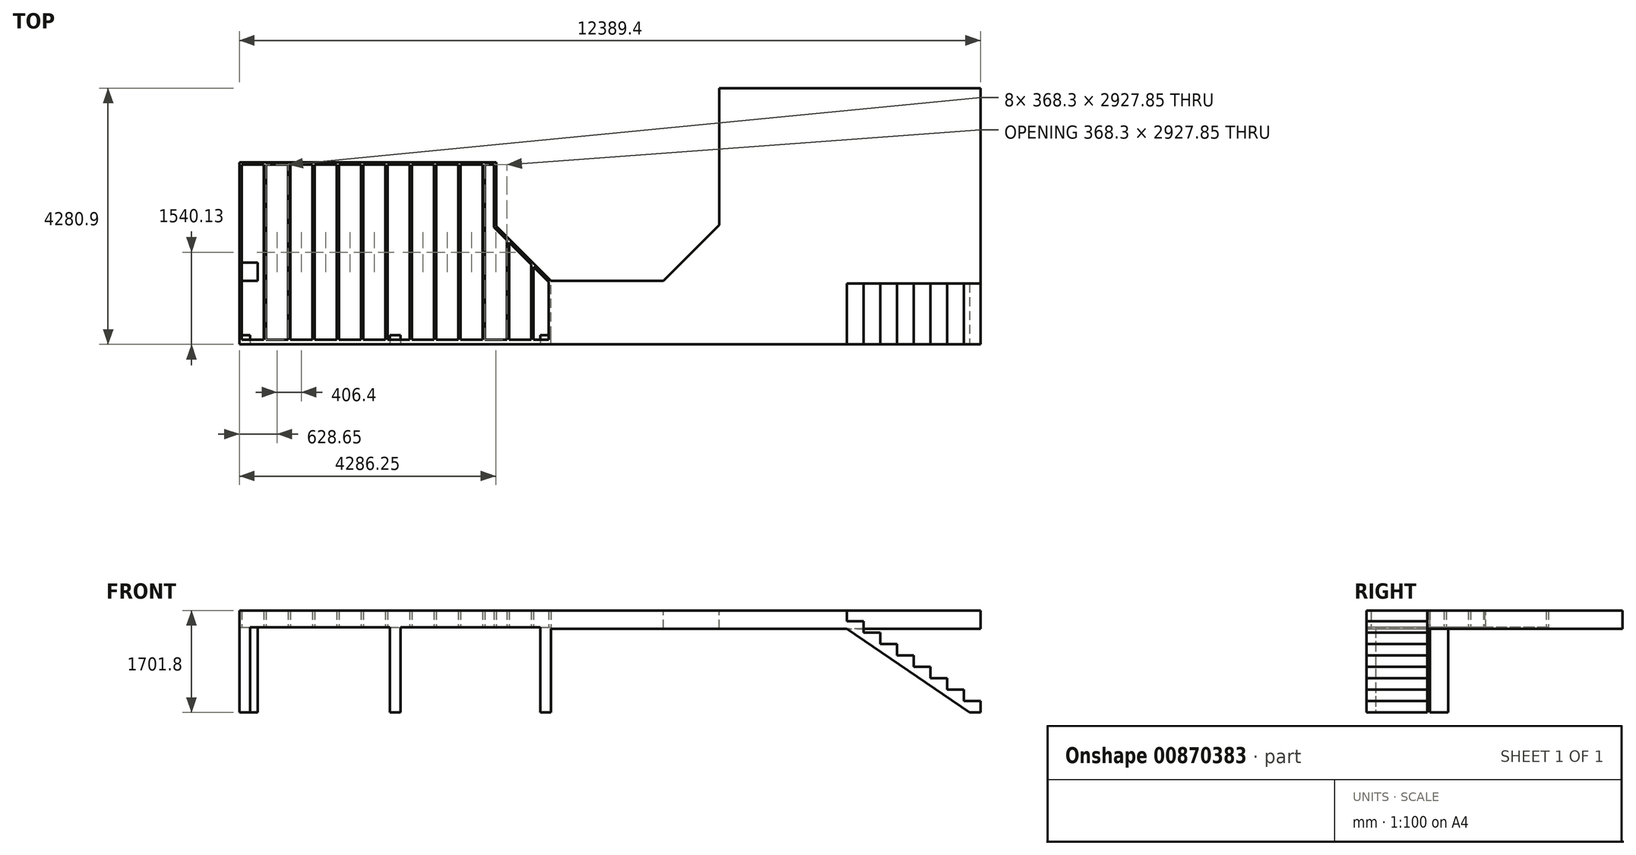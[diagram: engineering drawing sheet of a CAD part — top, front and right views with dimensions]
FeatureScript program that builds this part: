
annotation { "Feature Type Name" : "Feature", "Feature Type Description" : "" }
export const myFeature = defineFeature(function(context is Context, id is Id, definition is map)
    precondition{}
    {
        {
            var Q0;
            Q0=qCreatedBy(makeId("Top.planeOp"),FACE);
            var sketch = newSketch(context, id + "F0", { "sketchPlane" : qUnion([Q0])});
            skLineSegment(sketch, "E0.bottom", {"start": v(0, -1676.4) * mm, "end": v(304.8, -1676.4) * mm});
            skLineSegment(sketch, "E0.top", {"start": v(0, -1981.2) * mm, "end": v(304.8, -1981.2) * mm});
            skLineSegment(sketch, "E0.left", {"start": v(0, -1676.4) * mm, "end": v(0, -1981.2) * mm});
            skLineSegment(sketch, "E0.right", {"start": v(304.8, -1676.4) * mm, "end": v(304.8, -1981.2) * mm});
            skLineSegment(sketch, "E1.bottom", {"start": v(0, -2889.75) * mm, "end": v(177.8, -2889.75) * mm});
            skLineSegment(sketch, "E1.top", {"start": v(0, -3042.15) * mm, "end": v(177.8, -3042.15) * mm});
            skLineSegment(sketch, "E1.left", {"start": v(0, -2889.75) * mm, "end": v(0, -3042.15) * mm});
            skLineSegment(sketch, "E1.right", {"start": v(177.8, -2889.75) * mm, "end": v(177.8, -3042.15) * mm});
            skLineSegment(sketch, "E2.bottom", {"start": v(2514.6, -2889.75) * mm, "end": v(2692.4, -2889.75) * mm});
            skLineSegment(sketch, "E2.top", {"start": v(2514.6, -3042.15) * mm, "end": v(2692.4, -3042.15) * mm});
            skLineSegment(sketch, "E2.left", {"start": v(2514.6, -2889.75) * mm, "end": v(2514.6, -3042.15) * mm});
            skLineSegment(sketch, "E2.right", {"start": v(2692.4, -2889.75) * mm, "end": v(2692.4, -3042.15) * mm});
            skLineSegment(sketch, "E3.bottom", {"start": v(5029.2, -2889.75) * mm, "end": v(5207, -2889.75) * mm});
            skLineSegment(sketch, "E3.top", {"start": v(5029.2, -3042.15) * mm, "end": v(5207, -3042.15) * mm});
            skLineSegment(sketch, "E3.left", {"start": v(5029.2, -2889.75) * mm, "end": v(5029.2, -3042.15) * mm});
            skLineSegment(sketch, "E3.right", {"start": v(5207, -2889.75) * mm, "end": v(5207, -3042.15) * mm});
            skLineSegment(sketch, "E4", {"start": v(0, 0) * mm, "end": v(4292.6, 0) * mm, "construction": true});
            skLineSegment(sketch, "E5", {"start": v(4292.6, 0) * mm, "end": v(4292.6, -1066.8) * mm, "construction": true});
            skLineSegment(sketch, "E6", {"start": v(4292.6, -1066.8) * mm, "end": v(5226.55, -2000.75) * mm, "construction": true});
            skLineSegment(sketch, "E7", {"start": v(5226.55, -2000.75) * mm, "end": v(7106.15, -2000.75) * mm, "construction": true});
            skSolve(sketch);
        }
        {
            var Q0;
            Q0=qSketchRegion(id+"F0",true);
            extrude(context, id + "F1", {"entities" : qUnion([Q0]), "depth" : 1422.4 * mm, "offsetDistance" : 25.4 * mm});
        }
        {
            var Q0;
            Q0=makeQuery(id+"F1.opExtrude","CAP_FACE",FACE,{"disambiguationData":[OSD([sQuery(id+"F0.wireOp",EDGE,"E0.bottom"),sQuery(id+"F0.wireOp",EDGE,"E0.top"),sQuery(id+"F0.wireOp",EDGE,"E0.left"),sQuery(id+"F0.wireOp",EDGE,"E0.right")])],"isStart":false});
            var sketch = newSketch(context, id + "F2", { "sketchPlane" : qUnion([Q0])});
            skLineSegment(sketch, "E8.0", {"start": v(0, 0) * mm, "end": v(4292.6, 0) * mm});
            skLineSegment(sketch, "E9.0", {"start": v(4292.6, 0) * mm, "end": v(4292.6, -1066.8) * mm});
            skLineSegment(sketch, "E9.1", {"start": v(4292.6, -1066.8) * mm, "end": v(5207, -1981.2) * mm});
            skLineSegment(sketch, "E10", {"start": v(0, 0) * mm, "end": v(0, -3042.15) * mm});
            skLineSegment(sketch, "E11", {"start": v(0, -3042.15) * mm, "end": v(5207, -3042.15) * mm});
            skLineSegment(sketch, "E12", {"start": v(5207, -3042.15) * mm, "end": v(5207, -1981.2) * mm});
            skPoint(sketch, "E13.orphan", {"position": v(5226.55, -2000.75) * mm});
            skLineSegment(sketch, "E14.0", {"start": v(4254.5, -38.1) * mm, "end": v(4254.5, -1082.58) * mm});
            skLineSegment(sketch, "E14.1", {"start": v(5168.9, -3004.05) * mm, "end": v(5168.9, -1996.98) * mm});
            skLineSegment(sketch, "E14.2", {"start": v(38.1, -3004.05) * mm, "end": v(5168.9, -3004.05) * mm});
            skLineSegment(sketch, "E14.3", {"start": v(4254.5, -1082.58) * mm, "end": v(5168.9, -1996.98) * mm});
            skLineSegment(sketch, "E14.4", {"start": v(38.1, -38.1) * mm, "end": v(38.1, -3004.05) * mm});
            skLineSegment(sketch, "E14.5", {"start": v(38.1, -38.1) * mm, "end": v(4254.5, -38.1) * mm});
            skSolve(sketch);
        }
        {
            var Q0;
            Q0=qSketchRegion(id+"F2",true);
            extrude(context, id + "F3", {"entities" : qUnion([Q0]), "operationType" : NewBodyOperationType.ADD, "depth" : 279.4 * mm, "offsetDistance" : 25.4 * mm});
        }
        {
            var Q0;
            Q0=makeQuery(id+"F1.opExtrude","CAP_FACE",FACE,{"disambiguationData":[OSD([sQuery(id+"F0.wireOp",EDGE,"E1.bottom"),sQuery(id+"F0.wireOp",EDGE,"E1.top"),sQuery(id+"F0.wireOp",EDGE,"E1.left"),sQuery(id+"F0.wireOp",EDGE,"E1.right")])],"isStart":false});
            var sketch = newSketch(context, id + "F4", { "sketchPlane" : qUnion([Q0])});
            skPoint(sketch, "E15.oppositeSnap0", {"position": v(38.1, -2965.95) * mm});
            skLineSegment(sketch, "E15.bottom", {"start": v(38.1, -3004.05) * mm, "end": v(5168.9, -3004.05) * mm});
            skLineSegment(sketch, "E15.top", {"start": v(38.1, -2965.95) * mm, "end": v(5168.9, -2965.95) * mm});
            skLineSegment(sketch, "E15.left", {"start": v(38.1, -3004.05) * mm, "end": v(38.1, -2965.95) * mm});
            skLineSegment(sketch, "E15.right", {"start": v(5168.9, -3004.05) * mm, "end": v(5168.9, -2965.95) * mm});
            skSolve(sketch);
        }
        {
            var Q0;
            Q0=qSketchRegion(id+"F4",true);
            var Q1;
            Q1=makeQuery(id+"F3.opExtrude","CAP_FACE",FACE,{"disambiguationData":[OSD([sQuery(id+"F2.wireOp",EDGE,"E8.0"),sQuery(id+"F2.wireOp",EDGE,"E9.0"),sQuery(id+"F2.wireOp",EDGE,"E9.1"),sQuery(id+"F2.wireOp",EDGE,"E10"),sQuery(id+"F2.wireOp",EDGE,"E11"),sQuery(id+"F2.wireOp",EDGE,"E12"),sQuery(id+"F2.wireOp",EDGE,"E14.0"),sQuery(id+"F2.wireOp",EDGE,"E14.1"),sQuery(id+"F2.wireOp",EDGE,"E14.2"),sQuery(id+"F2.wireOp",EDGE,"E14.3"),sQuery(id+"F2.wireOp",EDGE,"E14.4"),sQuery(id+"F2.wireOp",EDGE,"E14.5")])],"isStart":false});
            extrude(context, id + "F5", {"entities" : qUnion([Q0]), "operationType" : NewBodyOperationType.ADD, "endBound" : BoundingType.UP_TO_SURFACE, "depth" : 25.4 * mm, "endBoundEntityFace" : qUnion([Q1]), "offsetDistance" : 25.4 * mm});
        }
        {
            var Q0;
            Q0=makeQuery(id+"F1.opExtrude","CAP_FACE",FACE,{"disambiguationData":[OSD([sQuery(id+"F0.wireOp",EDGE,"E0.bottom"),sQuery(id+"F0.wireOp",EDGE,"E0.top"),sQuery(id+"F0.wireOp",EDGE,"E0.left"),sQuery(id+"F0.wireOp",EDGE,"E0.right")])],"isStart":false});
            var sketch = newSketch(context, id + "F6", { "sketchPlane" : qUnion([Q0])});
            skLineSegment(sketch, "E16.bottom", {"start": v(406.4, -38.1) * mm, "end": v(444.5, -38.1) * mm});
            skLineSegment(sketch, "E16.top", {"start": v(406.4, -2965.95) * mm, "end": v(444.5, -2965.95) * mm});
            skLineSegment(sketch, "E16.left", {"start": v(406.4, -38.1) * mm, "end": v(406.4, -2965.95) * mm});
            skLineSegment(sketch, "E16.right", {"start": v(444.5, -38.1) * mm, "end": v(444.5, -2965.95) * mm});
            skLineSegment(sketch, "E17.1.0.0", {"start": v(850.9, -38.1) * mm, "end": v(850.9, -2965.95) * mm});
            skLineSegment(sketch, "E17.1.0.1", {"start": v(812.8, -38.1) * mm, "end": v(812.8, -2965.95) * mm});
            skLineSegment(sketch, "E17.1.0.2", {"start": v(812.8, -38.1) * mm, "end": v(850.9, -38.1) * mm});
            skLineSegment(sketch, "E17.1.0.3", {"start": v(812.8, -2965.95) * mm, "end": v(850.9, -2965.95) * mm});
            skLineSegment(sketch, "E17.2.0.0", {"start": v(1257.3, -38.1) * mm, "end": v(1257.3, -2965.95) * mm});
            skLineSegment(sketch, "E17.2.0.1", {"start": v(1219.2, -38.1) * mm, "end": v(1219.2, -2965.95) * mm});
            skLineSegment(sketch, "E17.2.0.2", {"start": v(1219.2, -38.1) * mm, "end": v(1257.3, -38.1) * mm});
            skLineSegment(sketch, "E17.2.0.3", {"start": v(1219.2, -2965.95) * mm, "end": v(1257.3, -2965.95) * mm});
            skLineSegment(sketch, "E17.3.0.0", {"start": v(1663.7, -38.1) * mm, "end": v(1663.7, -2965.95) * mm});
            skLineSegment(sketch, "E17.3.0.1", {"start": v(1625.6, -38.1) * mm, "end": v(1625.6, -2965.95) * mm});
            skLineSegment(sketch, "E17.3.0.2", {"start": v(1625.6, -38.1) * mm, "end": v(1663.7, -38.1) * mm});
            skLineSegment(sketch, "E17.3.0.3", {"start": v(1625.6, -2965.95) * mm, "end": v(1663.7, -2965.95) * mm});
            skLineSegment(sketch, "E17.4.0.0", {"start": v(2070.1, -38.1) * mm, "end": v(2070.1, -2965.95) * mm});
            skLineSegment(sketch, "E17.4.0.1", {"start": v(2032, -38.1) * mm, "end": v(2032, -2965.95) * mm});
            skLineSegment(sketch, "E17.4.0.2", {"start": v(2032, -38.1) * mm, "end": v(2070.1, -38.1) * mm});
            skLineSegment(sketch, "E17.4.0.3", {"start": v(2032, -2965.95) * mm, "end": v(2070.1, -2965.95) * mm});
            skLineSegment(sketch, "E17.5.0.0", {"start": v(2476.5, -38.1) * mm, "end": v(2476.5, -2965.95) * mm});
            skLineSegment(sketch, "E17.5.0.1", {"start": v(2438.4, -38.1) * mm, "end": v(2438.4, -2965.95) * mm});
            skLineSegment(sketch, "E17.5.0.2", {"start": v(2438.4, -38.1) * mm, "end": v(2476.5, -38.1) * mm});
            skLineSegment(sketch, "E17.5.0.3", {"start": v(2438.4, -2965.95) * mm, "end": v(2476.5, -2965.95) * mm});
            skLineSegment(sketch, "E17.6.0.0", {"start": v(2882.9, -38.1) * mm, "end": v(2882.9, -2965.95) * mm});
            skLineSegment(sketch, "E17.6.0.1", {"start": v(2844.8, -38.1) * mm, "end": v(2844.8, -2965.95) * mm});
            skLineSegment(sketch, "E17.6.0.2", {"start": v(2844.8, -38.1) * mm, "end": v(2882.9, -38.1) * mm});
            skLineSegment(sketch, "E17.6.0.3", {"start": v(2844.8, -2965.95) * mm, "end": v(2882.9, -2965.95) * mm});
            skLineSegment(sketch, "E17.7.0.0", {"start": v(3289.3, -38.1) * mm, "end": v(3289.3, -2965.95) * mm});
            skLineSegment(sketch, "E17.7.0.1", {"start": v(3251.2, -38.1) * mm, "end": v(3251.2, -2965.95) * mm});
            skLineSegment(sketch, "E17.7.0.2", {"start": v(3251.2, -38.1) * mm, "end": v(3289.3, -38.1) * mm});
            skLineSegment(sketch, "E17.7.0.3", {"start": v(3251.2, -2965.95) * mm, "end": v(3289.3, -2965.95) * mm});
            skLineSegment(sketch, "E17.8.0.0", {"start": v(3695.7, -38.1) * mm, "end": v(3695.7, -2965.95) * mm});
            skLineSegment(sketch, "E17.8.0.1", {"start": v(3657.6, -38.1) * mm, "end": v(3657.6, -2965.95) * mm});
            skLineSegment(sketch, "E17.8.0.2", {"start": v(3657.6, -38.1) * mm, "end": v(3695.7, -38.1) * mm});
            skLineSegment(sketch, "E17.8.0.3", {"start": v(3657.6, -2965.95) * mm, "end": v(3695.7, -2965.95) * mm});
            skLineSegment(sketch, "E17.9.0.0", {"start": v(4102.1, -38.1) * mm, "end": v(4102.1, -2965.95) * mm});
            skLineSegment(sketch, "E17.9.0.1", {"start": v(4064, -38.1) * mm, "end": v(4064, -2965.95) * mm});
            skLineSegment(sketch, "E17.9.0.2", {"start": v(4064, -38.1) * mm, "end": v(4102.1, -38.1) * mm});
            skLineSegment(sketch, "E17.9.0.3", {"start": v(4064, -2965.95) * mm, "end": v(4102.1, -2965.95) * mm});
            skLineSegment(sketch, "E17.direction1", {"start": v(406.4, -2965.95) * mm, "end": v(812.8, -2965.95) * mm, "construction": true});
            skLineSegment(sketch, "E18.top", {"start": v(4470.4, -2965.95) * mm, "end": v(4508.5, -2965.95) * mm});
            skLineSegment(sketch, "E18.left", {"start": v(4470.4, -1298.48) * mm, "end": v(4470.4, -2965.95) * mm});
            skLineSegment(sketch, "E18.right", {"start": v(4508.5, -1336.58) * mm, "end": v(4508.5, -2965.95) * mm});
            skLineSegment(sketch, "E19.top", {"start": v(4876.8, -2965.95) * mm, "end": v(4914.9, -2965.95) * mm});
            skLineSegment(sketch, "E19.left", {"start": v(4876.8, -1704.88) * mm, "end": v(4876.8, -2965.95) * mm});
            skLineSegment(sketch, "E19.right", {"start": v(4914.9, -1742.98) * mm, "end": v(4914.9, -2965.95) * mm});
            skLineSegment(sketch, "E20", {"start": v(4470.4, -1298.48) * mm, "end": v(4508.5, -1336.58) * mm});
            skLineSegment(sketch, "E21.trimOffspring", {"start": v(4876.8, -1704.88) * mm, "end": v(4914.9, -1742.98) * mm});
            skSolve(sketch);
        }
        {
            var Q0;
            Q0=qSketchRegion(id+"F6",true);
            var Q1;
            {var subQ0=sQuery(id+"F2.wireOp",EDGE,"E14.5");var subQ1=sQuery(id+"F2.wireOp",EDGE,"E14.4");var subQ2=sQuery(id+"F2.wireOp",EDGE,"E14.3");var subQ3=sQuery(id+"F2.wireOp",EDGE,"E14.2");var subQ4=sQuery(id+"F2.wireOp",EDGE,"E14.1");var subQ5=sQuery(id+"F2.wireOp",EDGE,"E14.0");var subQ6=sQuery(id+"F2.wireOp",EDGE,"E12");var subQ7=sQuery(id+"F2.wireOp",EDGE,"E11");var subQ8=sQuery(id+"F2.wireOp",EDGE,"E10");var subQ9=sQuery(id+"F2.wireOp",EDGE,"E9.1");var subQ10=sQuery(id+"F2.wireOp",EDGE,"E9.0");var subQ11=sQuery(id+"F2.wireOp",EDGE,"E8.0");Q1=makeQuery(id+"F5.boolean.opBoolean","MERGE",FACE,{"derivedFrom":[makeQuery(id+"F3.opExtrude","CAP_FACE",FACE,{"disambiguationData":[OSD([subQ11,subQ10,subQ9,subQ8,subQ7,subQ6,subQ5,subQ4,subQ3,subQ2,subQ1,subQ0])],"isStart":false}),makeQuery(id+"F5.opExtrude","CAP_FACE",FACE,{"disambiguationData":[OSD([subQ11,subQ10,subQ9,subQ8,subQ7,subQ6,subQ5,subQ4,subQ3,subQ2,subQ1,subQ0])],"isStart":false})]});}
            extrude(context, id + "F7", {"entities" : qUnion([Q0]), "operationType" : NewBodyOperationType.ADD, "endBound" : BoundingType.UP_TO_SURFACE, "depth" : 25.4 * mm, "endBoundEntityFace" : qUnion([Q1]), "offsetDistance" : 25.4 * mm});
        }
        {
            var Q0;
            Q0=makeQuery(id+"F7.boolean.opBoolean","MERGE",FACE,{"derivedFrom":[makeQuery(id+"F5.boolean.opBoolean","MERGE",FACE,{"derivedFrom":[makeQuery(id+"F3.opExtrude","CAP_FACE",FACE,{"disambiguationData":[OSD([sQuery(id+"F2.wireOp",EDGE,"E8.0"),sQuery(id+"F2.wireOp",EDGE,"E9.0"),sQuery(id+"F2.wireOp",EDGE,"E9.1"),sQuery(id+"F2.wireOp",EDGE,"E10"),sQuery(id+"F2.wireOp",EDGE,"E11"),sQuery(id+"F2.wireOp",EDGE,"E12"),sQuery(id+"F2.wireOp",EDGE,"E14.0"),sQuery(id+"F2.wireOp",EDGE,"E14.1"),sQuery(id+"F2.wireOp",EDGE,"E14.2"),sQuery(id+"F2.wireOp",EDGE,"E14.3"),sQuery(id+"F2.wireOp",EDGE,"E14.4"),sQuery(id+"F2.wireOp",EDGE,"E14.5")])],"isStart":false}),makeQuery(id+"F5.opExtrude","CAP_FACE",FACE,{"disambiguationData":[OSD([sQuery(id+"F4.wireOp",EDGE,"E15.bottom"),sQuery(id+"F4.wireOp",EDGE,"E15.top"),sQuery(id+"F4.wireOp",EDGE,"E15.left"),sQuery(id+"F4.wireOp",EDGE,"E15.right")])],"isStart":false})]}),makeQuery(id+"F7.opExtrude","CAP_FACE",FACE,{"disambiguationData":[OSD([sQuery(id+"F6.wireOp",EDGE,"E16.bottom"),sQuery(id+"F6.wireOp",EDGE,"E16.top"),sQuery(id+"F6.wireOp",EDGE,"E16.left"),sQuery(id+"F6.wireOp",EDGE,"E16.right")])],"isStart":false}),makeQuery(id+"F7.opExtrude","CAP_FACE",FACE,{"disambiguationData":[OSD([sQuery(id+"F6.wireOp",EDGE,"E17.1.0.0"),sQuery(id+"F6.wireOp",EDGE,"E17.1.0.1"),sQuery(id+"F6.wireOp",EDGE,"E17.1.0.2"),sQuery(id+"F6.wireOp",EDGE,"E17.1.0.3")])],"isStart":false}),makeQuery(id+"F7.opExtrude","CAP_FACE",FACE,{"disambiguationData":[OSD([sQuery(id+"F6.wireOp",EDGE,"E17.2.0.0"),sQuery(id+"F6.wireOp",EDGE,"E17.2.0.1"),sQuery(id+"F6.wireOp",EDGE,"E17.2.0.2"),sQuery(id+"F6.wireOp",EDGE,"E17.2.0.3")])],"isStart":false}),makeQuery(id+"F7.opExtrude","CAP_FACE",FACE,{"disambiguationData":[OSD([sQuery(id+"F6.wireOp",EDGE,"E17.3.0.0"),sQuery(id+"F6.wireOp",EDGE,"E17.3.0.1"),sQuery(id+"F6.wireOp",EDGE,"E17.3.0.2"),sQuery(id+"F6.wireOp",EDGE,"E17.3.0.3")])],"isStart":false}),makeQuery(id+"F7.opExtrude","CAP_FACE",FACE,{"disambiguationData":[OSD([sQuery(id+"F6.wireOp",EDGE,"E17.4.0.0"),sQuery(id+"F6.wireOp",EDGE,"E17.4.0.1"),sQuery(id+"F6.wireOp",EDGE,"E17.4.0.2"),sQuery(id+"F6.wireOp",EDGE,"E17.4.0.3")])],"isStart":false}),makeQuery(id+"F7.opExtrude","CAP_FACE",FACE,{"disambiguationData":[OSD([sQuery(id+"F6.wireOp",EDGE,"E17.5.0.0"),sQuery(id+"F6.wireOp",EDGE,"E17.5.0.1"),sQuery(id+"F6.wireOp",EDGE,"E17.5.0.2"),sQuery(id+"F6.wireOp",EDGE,"E17.5.0.3")])],"isStart":false}),makeQuery(id+"F7.opExtrude","CAP_FACE",FACE,{"disambiguationData":[OSD([sQuery(id+"F6.wireOp",EDGE,"E17.6.0.0"),sQuery(id+"F6.wireOp",EDGE,"E17.6.0.1"),sQuery(id+"F6.wireOp",EDGE,"E17.6.0.2"),sQuery(id+"F6.wireOp",EDGE,"E17.6.0.3")])],"isStart":false}),makeQuery(id+"F7.opExtrude","CAP_FACE",FACE,{"disambiguationData":[OSD([sQuery(id+"F6.wireOp",EDGE,"E17.7.0.0"),sQuery(id+"F6.wireOp",EDGE,"E17.7.0.1"),sQuery(id+"F6.wireOp",EDGE,"E17.7.0.2"),sQuery(id+"F6.wireOp",EDGE,"E17.7.0.3")])],"isStart":false}),makeQuery(id+"F7.opExtrude","CAP_FACE",FACE,{"disambiguationData":[OSD([sQuery(id+"F6.wireOp",EDGE,"E17.8.0.0"),sQuery(id+"F6.wireOp",EDGE,"E17.8.0.1"),sQuery(id+"F6.wireOp",EDGE,"E17.8.0.2"),sQuery(id+"F6.wireOp",EDGE,"E17.8.0.3")])],"isStart":false}),makeQuery(id+"F7.opExtrude","CAP_FACE",FACE,{"disambiguationData":[OSD([sQuery(id+"F6.wireOp",EDGE,"E17.9.0.0"),sQuery(id+"F6.wireOp",EDGE,"E17.9.0.1"),sQuery(id+"F6.wireOp",EDGE,"E17.9.0.2"),sQuery(id+"F6.wireOp",EDGE,"E17.9.0.3")])],"isStart":false}),makeQuery(id+"F7.opExtrude","CAP_FACE",FACE,{"disambiguationData":[OSD([sQuery(id+"F6.wireOp",EDGE,"E18.top"),sQuery(id+"F6.wireOp",EDGE,"E18.left"),sQuery(id+"F6.wireOp",EDGE,"E18.right"),sQuery(id+"F6.wireOp",EDGE,"E20")])],"isStart":false}),makeQuery(id+"F7.opExtrude","CAP_FACE",FACE,{"disambiguationData":[OSD([sQuery(id+"F6.wireOp",EDGE,"E19.top"),sQuery(id+"F6.wireOp",EDGE,"E19.left"),sQuery(id+"F6.wireOp",EDGE,"E19.right"),sQuery(id+"F6.wireOp",EDGE,"E21.trimOffspring")])],"isStart":false})]});
            var sketch = newSketch(context, id + "F8", { "sketchPlane" : qUnion([Q0])});
            skLineSegment(sketch, "E22", {"start": v(5207, -1981.2) * mm, "end": v(5207, -3042.15) * mm});
            skLineSegment(sketch, "E23", {"start": v(5207, -1981.2) * mm, "end": v(7086.6, -1981.2) * mm});
            skLineSegment(sketch, "E24", {"start": v(7086.6, -1981.2) * mm, "end": v(8020.55, -1047.25) * mm});
            skLineSegment(sketch, "E25", {"start": v(8020.55, -1047.25) * mm, "end": v(8020.55, 1238.75) * mm});
            skLineSegment(sketch, "E26", {"start": v(8020.55, 1238.75) * mm, "end": v(12389.35, 1238.75) * mm});
            skLineSegment(sketch, "E27", {"start": v(12389.35, 1238.75) * mm, "end": v(12389.35, -3042.15) * mm});
            skLineSegment(sketch, "E28", {"start": v(5207, -3042.15) * mm, "end": v(12389.35, -3042.15) * mm});
            skSolve(sketch);
        }
        {
            var Q0;
            Q0=qSketchRegion(id+"F8",true);
            extrude(context, id + "F9", {"entities" : qUnion([Q0]), "operationType" : NewBodyOperationType.ADD, "oppositeDirection" : true, "depth" : 304.8 * mm, "offsetDistance" : 25.4 * mm});
        }
        {
            var Q0;
            Q0=makeQuery(id+"F9.boolean.opBoolean","MERGE",FACE,{"derivedFrom":[makeQuery(id+"F7.boolean.opBoolean","MERGE",FACE,{"derivedFrom":[makeQuery(id+"F5.boolean.opBoolean","MERGE",FACE,{"derivedFrom":[makeQuery(id+"F3.opExtrude","CAP_FACE",FACE,{"disambiguationData":[OSD([sQuery(id+"F2.wireOp",EDGE,"E8.0"),sQuery(id+"F2.wireOp",EDGE,"E9.0"),sQuery(id+"F2.wireOp",EDGE,"E9.1"),sQuery(id+"F2.wireOp",EDGE,"E10"),sQuery(id+"F2.wireOp",EDGE,"E11"),sQuery(id+"F2.wireOp",EDGE,"E12"),sQuery(id+"F2.wireOp",EDGE,"E14.0"),sQuery(id+"F2.wireOp",EDGE,"E14.1"),sQuery(id+"F2.wireOp",EDGE,"E14.2"),sQuery(id+"F2.wireOp",EDGE,"E14.3"),sQuery(id+"F2.wireOp",EDGE,"E14.4"),sQuery(id+"F2.wireOp",EDGE,"E14.5")])],"isStart":false}),makeQuery(id+"F5.opExtrude","CAP_FACE",FACE,{"disambiguationData":[OSD([sQuery(id+"F4.wireOp",EDGE,"E15.bottom"),sQuery(id+"F4.wireOp",EDGE,"E15.top"),sQuery(id+"F4.wireOp",EDGE,"E15.left"),sQuery(id+"F4.wireOp",EDGE,"E15.right")])],"isStart":false})]}),makeQuery(id+"F7.opExtrude","CAP_FACE",FACE,{"disambiguationData":[OSD([sQuery(id+"F6.wireOp",EDGE,"E16.bottom"),sQuery(id+"F6.wireOp",EDGE,"E16.top"),sQuery(id+"F6.wireOp",EDGE,"E16.left"),sQuery(id+"F6.wireOp",EDGE,"E16.right")])],"isStart":false}),makeQuery(id+"F7.opExtrude","CAP_FACE",FACE,{"disambiguationData":[OSD([sQuery(id+"F6.wireOp",EDGE,"E17.1.0.0"),sQuery(id+"F6.wireOp",EDGE,"E17.1.0.1"),sQuery(id+"F6.wireOp",EDGE,"E17.1.0.2"),sQuery(id+"F6.wireOp",EDGE,"E17.1.0.3")])],"isStart":false}),makeQuery(id+"F7.opExtrude","CAP_FACE",FACE,{"disambiguationData":[OSD([sQuery(id+"F6.wireOp",EDGE,"E17.2.0.0"),sQuery(id+"F6.wireOp",EDGE,"E17.2.0.1"),sQuery(id+"F6.wireOp",EDGE,"E17.2.0.2"),sQuery(id+"F6.wireOp",EDGE,"E17.2.0.3")])],"isStart":false}),makeQuery(id+"F7.opExtrude","CAP_FACE",FACE,{"disambiguationData":[OSD([sQuery(id+"F6.wireOp",EDGE,"E17.3.0.0"),sQuery(id+"F6.wireOp",EDGE,"E17.3.0.1"),sQuery(id+"F6.wireOp",EDGE,"E17.3.0.2"),sQuery(id+"F6.wireOp",EDGE,"E17.3.0.3")])],"isStart":false}),makeQuery(id+"F7.opExtrude","CAP_FACE",FACE,{"disambiguationData":[OSD([sQuery(id+"F6.wireOp",EDGE,"E17.4.0.0"),sQuery(id+"F6.wireOp",EDGE,"E17.4.0.1"),sQuery(id+"F6.wireOp",EDGE,"E17.4.0.2"),sQuery(id+"F6.wireOp",EDGE,"E17.4.0.3")])],"isStart":false}),makeQuery(id+"F7.opExtrude","CAP_FACE",FACE,{"disambiguationData":[OSD([sQuery(id+"F6.wireOp",EDGE,"E17.5.0.0"),sQuery(id+"F6.wireOp",EDGE,"E17.5.0.1"),sQuery(id+"F6.wireOp",EDGE,"E17.5.0.2"),sQuery(id+"F6.wireOp",EDGE,"E17.5.0.3")])],"isStart":false}),makeQuery(id+"F7.opExtrude","CAP_FACE",FACE,{"disambiguationData":[OSD([sQuery(id+"F6.wireOp",EDGE,"E17.6.0.0"),sQuery(id+"F6.wireOp",EDGE,"E17.6.0.1"),sQuery(id+"F6.wireOp",EDGE,"E17.6.0.2"),sQuery(id+"F6.wireOp",EDGE,"E17.6.0.3")])],"isStart":false}),makeQuery(id+"F7.opExtrude","CAP_FACE",FACE,{"disambiguationData":[OSD([sQuery(id+"F6.wireOp",EDGE,"E17.7.0.0"),sQuery(id+"F6.wireOp",EDGE,"E17.7.0.1"),sQuery(id+"F6.wireOp",EDGE,"E17.7.0.2"),sQuery(id+"F6.wireOp",EDGE,"E17.7.0.3")])],"isStart":false}),makeQuery(id+"F7.opExtrude","CAP_FACE",FACE,{"disambiguationData":[OSD([sQuery(id+"F6.wireOp",EDGE,"E17.8.0.0"),sQuery(id+"F6.wireOp",EDGE,"E17.8.0.1"),sQuery(id+"F6.wireOp",EDGE,"E17.8.0.2"),sQuery(id+"F6.wireOp",EDGE,"E17.8.0.3")])],"isStart":false}),makeQuery(id+"F7.opExtrude","CAP_FACE",FACE,{"disambiguationData":[OSD([sQuery(id+"F6.wireOp",EDGE,"E17.9.0.0"),sQuery(id+"F6.wireOp",EDGE,"E17.9.0.1"),sQuery(id+"F6.wireOp",EDGE,"E17.9.0.2"),sQuery(id+"F6.wireOp",EDGE,"E17.9.0.3")])],"isStart":false}),makeQuery(id+"F7.opExtrude","CAP_FACE",FACE,{"disambiguationData":[OSD([sQuery(id+"F6.wireOp",EDGE,"E18.top"),sQuery(id+"F6.wireOp",EDGE,"E18.left"),sQuery(id+"F6.wireOp",EDGE,"E18.right"),sQuery(id+"F6.wireOp",EDGE,"E20")])],"isStart":false}),makeQuery(id+"F7.opExtrude","CAP_FACE",FACE,{"disambiguationData":[OSD([sQuery(id+"F6.wireOp",EDGE,"E19.top"),sQuery(id+"F6.wireOp",EDGE,"E19.left"),sQuery(id+"F6.wireOp",EDGE,"E19.right"),sQuery(id+"F6.wireOp",EDGE,"E21.trimOffspring")])],"isStart":false})]}),makeQuery(id+"F9.opExtrude","CAP_FACE",FACE,{"disambiguationData":[OSD([sQuery(id+"F8.wireOp",EDGE,"E22"),sQuery(id+"F8.wireOp",EDGE,"E23"),sQuery(id+"F8.wireOp",EDGE,"E24"),sQuery(id+"F8.wireOp",EDGE,"E25"),sQuery(id+"F8.wireOp",EDGE,"E26"),sQuery(id+"F8.wireOp",EDGE,"E27"),sQuery(id+"F8.wireOp",EDGE,"E28")])],"isStart":true})]});
            var sketch = newSketch(context, id + "F10", { "sketchPlane" : qUnion([Q0])});
            skLineSegment(sketch, "E29.bottom", {"start": v(12389.35, -3042.15) * mm, "end": v(10154.15, -3042.15) * mm});
            skLineSegment(sketch, "E29.top", {"start": v(12389.35, -2026.15) * mm, "end": v(10154.15, -2026.15) * mm});
            skLineSegment(sketch, "E29.left", {"start": v(12389.35, -3042.15) * mm, "end": v(12389.35, -2026.15) * mm});
            skLineSegment(sketch, "E29.right", {"start": v(10154.15, -3042.15) * mm, "end": v(10154.15, -2026.15) * mm});
            skSolve(sketch);
        }
        {
            var Q0;
            Q0=qSketchRegion(id+"F10",true);
            extrude(context, id + "F11", {"entities" : qUnion([Q0]), "operationType" : NewBodyOperationType.REMOVE, "endBound" : BoundingType.THROUGH_ALL, "oppositeDirection" : true, "depth" : 25.4 * mm, "offsetDistance" : 25.4 * mm});
        }
        {
            var Q0;
            Q0=makeQuery(id+"F9.boolean.opBoolean","MERGE",FACE,{"derivedFrom":[makeQuery(id+"F3.boolean.opBoolean","MERGE",FACE,{"derivedFrom":[makeQuery(id+"F1.opExtrude","SWEPT_FACE",FACE,{"disambiguationData":[OSD([sQuery(id+"F0.wireOp",EDGE,"E1.top")])]}),makeQuery(id+"F1.opExtrude","SWEPT_FACE",FACE,{"disambiguationData":[OSD([sQuery(id+"F0.wireOp",EDGE,"E2.top")])]}),makeQuery(id+"F1.opExtrude","SWEPT_FACE",FACE,{"disambiguationData":[OSD([sQuery(id+"F0.wireOp",EDGE,"E3.top")])]}),makeQuery(id+"F3.opExtrude","SWEPT_FACE",FACE,{"disambiguationData":[OSD([sQuery(id+"F2.wireOp",EDGE,"E11")])]})]}),makeQuery(id+"F9.opExtrude","SWEPT_FACE",FACE,{"disambiguationData":[OSD([sQuery(id+"F8.wireOp",EDGE,"E28")])]})]});
            var sketch = newSketch(context, id + "F12", { "sketchPlane" : qUnion([Q0])});
            skLineSegment(sketch, "E30", {"start": v(10154.15, 1701.8) * mm, "end": v(10154.15, 1524) * mm});
            skLineSegment(sketch, "E31", {"start": v(10154.15, 1524) * mm, "end": v(10433.55, 1524) * mm});
            skLineSegment(sketch, "E32", {"start": v(10433.55, 1524) * mm, "end": v(10433.55, 1333.5) * mm});
            skLineSegment(sketch, "E33", {"start": v(10433.55, 1333.5) * mm, "end": v(10712.95, 1333.5) * mm});
            skLineSegment(sketch, "E34", {"start": v(10712.95, 1333.5) * mm, "end": v(10712.95, 1143) * mm});
            skLineSegment(sketch, "E35", {"start": v(10712.95, 1143) * mm, "end": v(10992.35, 1143) * mm});
            skLineSegment(sketch, "E36", {"start": v(10992.35, 1143) * mm, "end": v(10992.35, 952.5) * mm});
            skLineSegment(sketch, "E37", {"start": v(10992.35, 952.5) * mm, "end": v(11271.75, 952.5) * mm});
            skLineSegment(sketch, "E38", {"start": v(11271.75, 952.5) * mm, "end": v(11271.75, 762) * mm});
            skLineSegment(sketch, "E39", {"start": v(11271.75, 762) * mm, "end": v(11551.15, 762) * mm});
            skLineSegment(sketch, "E40", {"start": v(11551.15, 762) * mm, "end": v(11551.15, 571.5) * mm});
            skLineSegment(sketch, "E41", {"start": v(11551.15, 571.5) * mm, "end": v(11830.55, 571.5) * mm});
            skLineSegment(sketch, "E42", {"start": v(11830.55, 571.5) * mm, "end": v(11830.55, 381) * mm});
            skLineSegment(sketch, "E43", {"start": v(11830.55, 381) * mm, "end": v(12109.95, 381) * mm});
            skLineSegment(sketch, "E44", {"start": v(12109.95, 381) * mm, "end": v(12109.95, 190.5) * mm});
            skLineSegment(sketch, "E45", {"start": v(12109.95, 190.5) * mm, "end": v(12389.35, 190.5) * mm});
            skLineSegment(sketch, "E46", {"start": v(12389.35, 190.5) * mm, "end": v(12389.35, 0) * mm});
            skLineSegment(sketch, "E47", {"start": v(12389.35, 0) * mm, "end": v(12206.4, 0) * mm});
            skLineSegment(sketch, "E48", {"start": v(12206.4, 0) * mm, "end": v(9710.44, 1701.8) * mm});
            skLineSegment(sketch, "E49", {"start": v(9710.44, 1701.8) * mm, "end": v(10154.15, 1701.8) * mm});
            skLineSegment(sketch, "E50", {"start": v(12389.35, 190.5) * mm, "end": v(10433.55, 1524) * mm, "construction": true});
            skPoint(sketch, "E51", {"position": v(12297.88, 0) * mm});
            skSolve(sketch);
        }
        {
            var Q0;
            Q0=qSketchRegion(id+"F12",true);
            var Q1;
            Q1=makeQuery(id+"F11.boolean.opBoolean","COPY",FACE,{"derivedFrom":makeQuery(id+"F11.opExtrude","SWEPT_FACE",FACE,{"disambiguationData":[OSD([sQuery(id+"F10.wireOp",EDGE,"E29.top")])]})});
            extrude(context, id + "F13", {"entities" : qUnion([Q0]), "operationType" : NewBodyOperationType.ADD, "endBound" : BoundingType.UP_TO_SURFACE, "oppositeDirection" : true, "depth" : 25.4 * mm, "endBoundEntityFace" : qUnion([Q1]), "offsetDistance" : 25.4 * mm});
        }
    });
